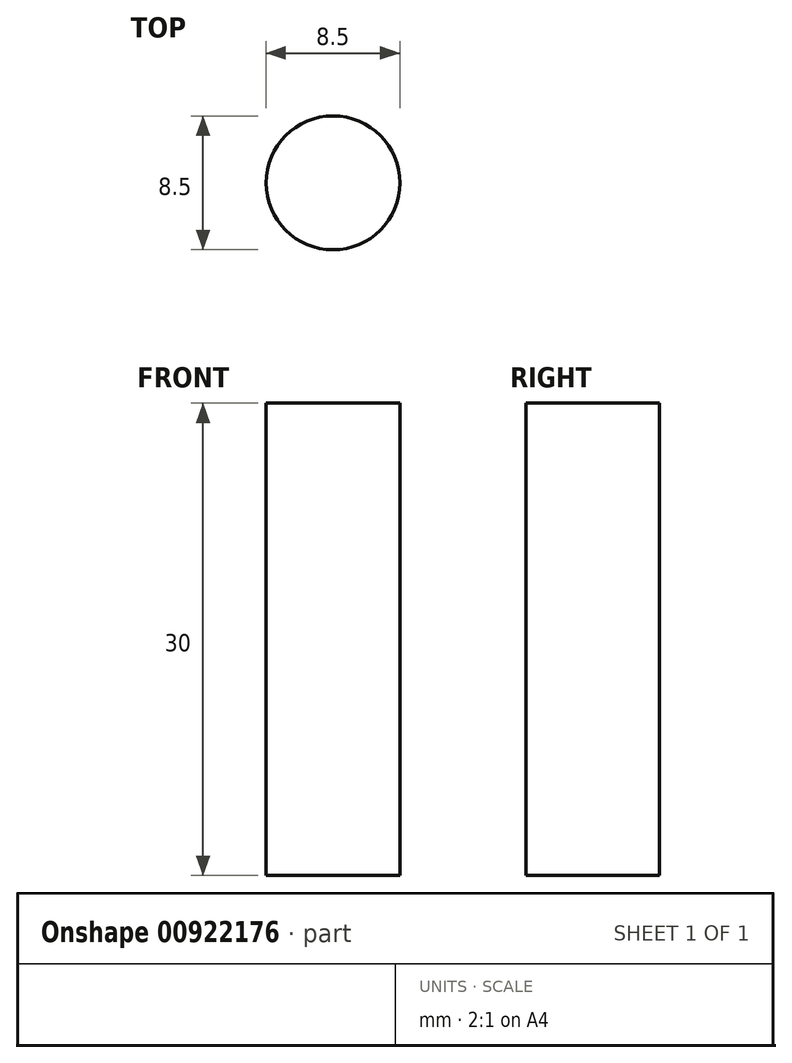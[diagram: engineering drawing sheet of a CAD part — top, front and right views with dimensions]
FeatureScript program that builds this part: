
annotation { "Feature Type Name" : "Feature", "Feature Type Description" : "" }
export const myFeature = defineFeature(function(context is Context, id is Id, definition is map)
    precondition{}
    {
        {
            var Q0;
            Q0=qCreatedBy(makeId("Top.planeOp"),FACE);
            var sketch = newSketch(context, id + "F0", { "sketchPlane" : qUnion([Q0])});
            skCircle(sketch, "E0", {"center": v(0, 0) * mm, "radius": 4.25 * mm});
            skSolve(sketch);
        }
        {
            var Q0;
            Q0 = qSketchRegion(id + "F0", true);
            extrude(context, id + "F1", {"entities" : qUnion([Q0]), "oppositeDirection" : true, "depth" : 30 * mm, "offsetDistance" : 25 * mm});
        }
    });
